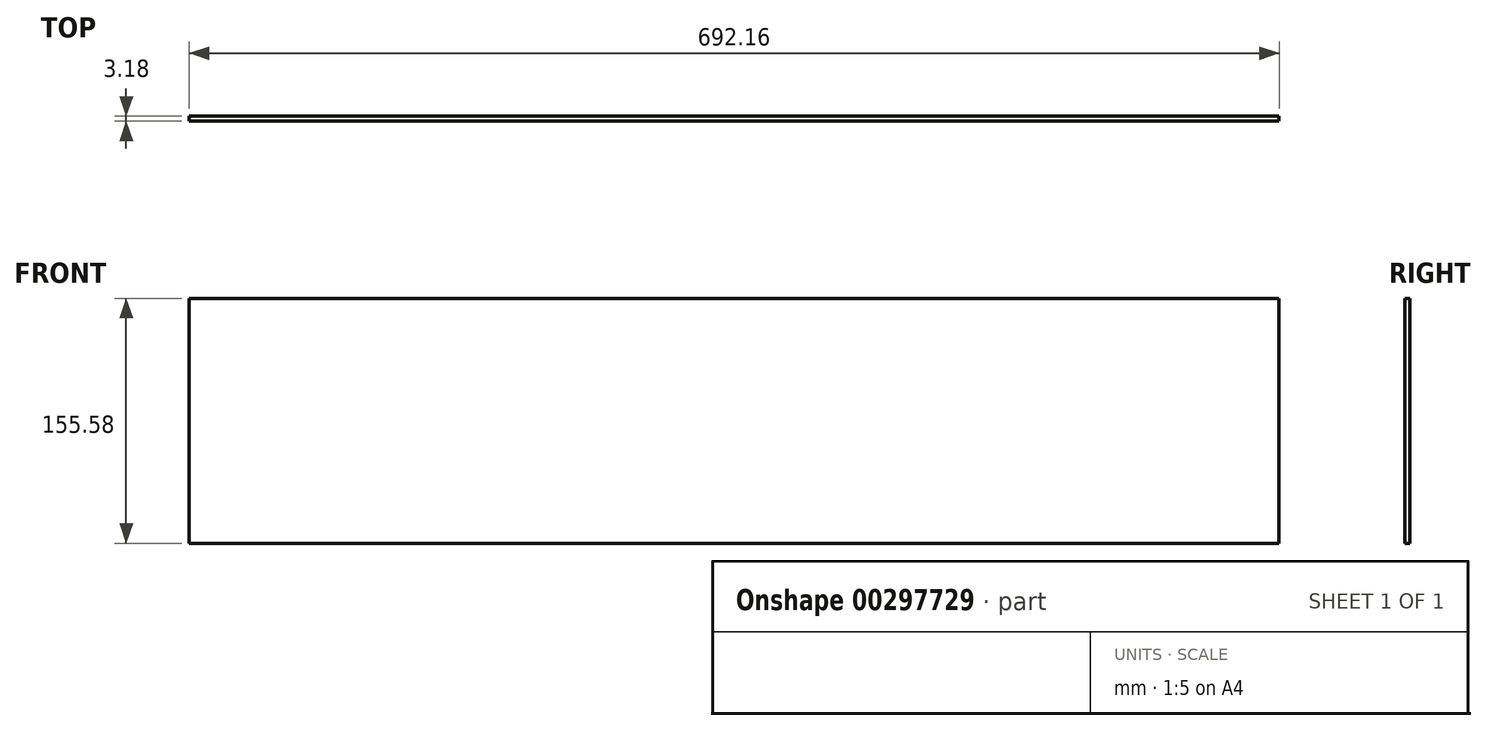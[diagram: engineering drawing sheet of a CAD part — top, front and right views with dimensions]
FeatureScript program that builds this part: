
annotation { "Feature Type Name" : "Feature", "Feature Type Description" : "" }
export const myFeature = defineFeature(function(context is Context, id is Id, definition is map)
    precondition{}
    {
        {
            var Q0;
            Q0=qCreatedBy(makeId("Front.planeOp"),FACE);
            var sketch = newSketch(context, id + "F0", { "sketchPlane" : qUnion([Q0])});
            skLineSegment(sketch, "E0.bottom", {"start": v(346.08, -77.79) * mm, "end": v(-346.08, -77.79) * mm});
            skLineSegment(sketch, "E0.top", {"start": v(346.08, 77.79) * mm, "end": v(-346.08, 77.79) * mm});
            skLineSegment(sketch, "E0.left", {"start": v(346.08, -77.79) * mm, "end": v(346.08, 77.79) * mm});
            skLineSegment(sketch, "E0.right", {"start": v(-346.08, -77.79) * mm, "end": v(-346.08, 77.79) * mm});
            skPoint(sketch, "E0.middle", {"position": v(0, 0) * mm});
            skSolve(sketch);
        }
        {
            var Q0;
            Q0 = qSketchRegion(id + "F0", true);
            extrude(context, id + "F1", {"entities" : qUnion([Q0]), "endBound" : BoundingType.SYMMETRIC, "depth" : 3.17 * mm});
        }
    });
